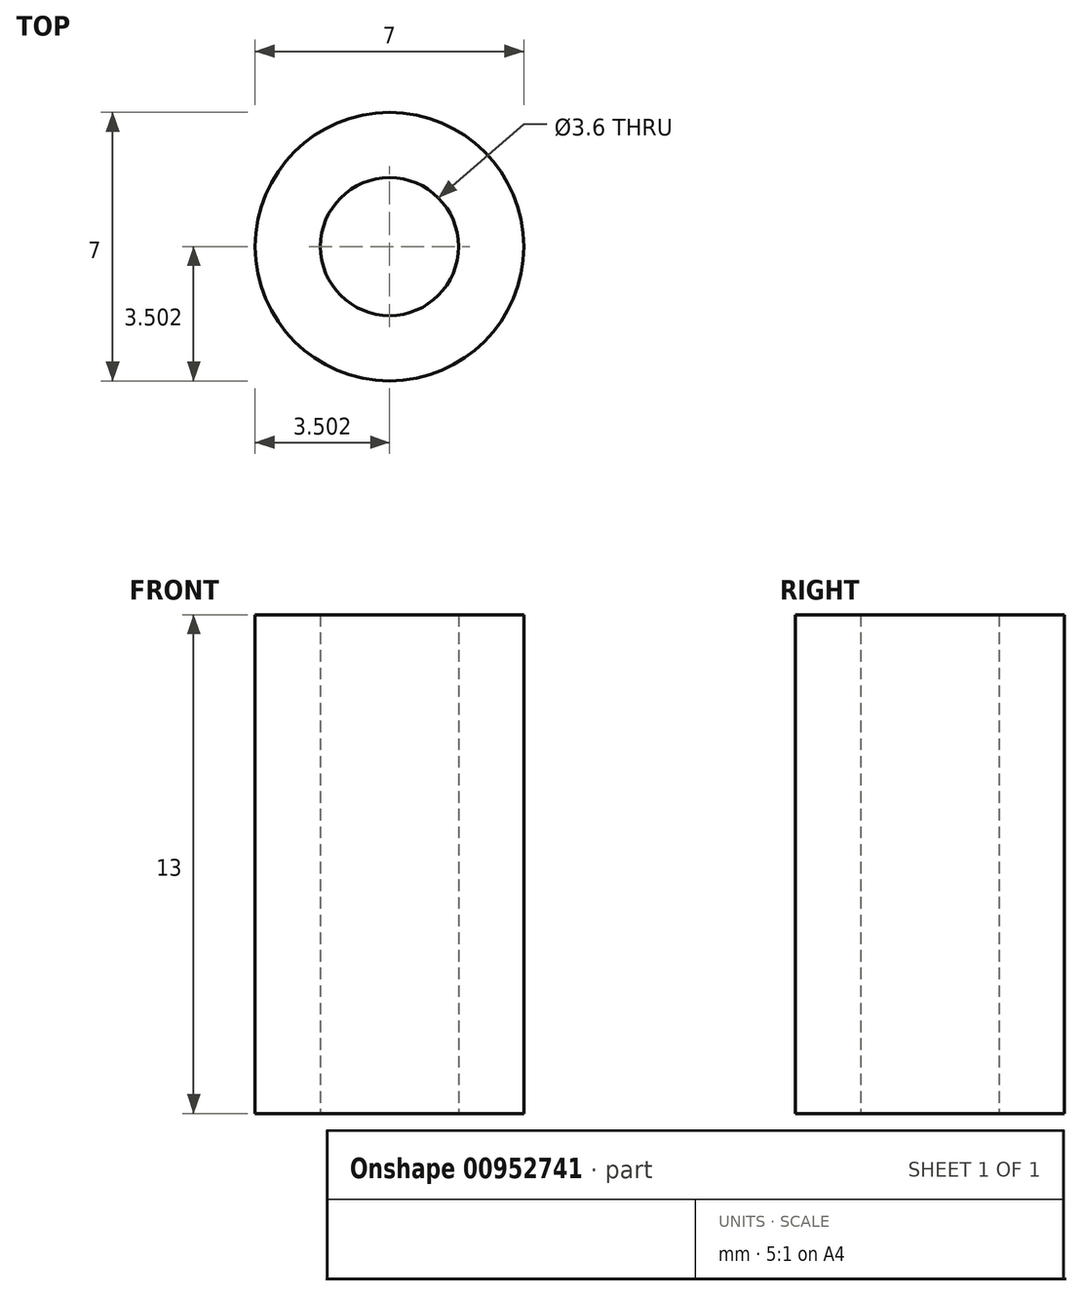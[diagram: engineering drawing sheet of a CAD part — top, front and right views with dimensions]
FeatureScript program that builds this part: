
annotation { "Feature Type Name" : "Feature", "Feature Type Description" : "" }
export const myFeature = defineFeature(function(context is Context, id is Id, definition is map)
    precondition{}
    {
        {
            var Q0;
            Q0=qCreatedBy(makeId("Top.planeOp"),FACE);
            var sketch = newSketch(context, id + "F0", { "sketchPlane" : qUnion([Q0])});
            skCircle(sketch, "E0", {"center": v(-38.23, 20.6) * mm, "radius": 1.8 * mm});
            skCircle(sketch, "E1", {"center": v(-38.23, 20.6) * mm, "radius": 3.5 * mm});
            skSolve(sketch);
        }
        {
            var Q0;
            Q0=makeQuery(id+"F0.imprint","IMPRINT",FACE,{"disambiguationData":[TD([[makeQuery(id+"F0.imprint","IMPRINT",EDGE,{"derivedFrom":sQuery(id+"F0.wireOp",EDGE,"E0")}),-1.0]])]});
            extrude(context, id + "F1", {"entities" : qUnion([Q0]), "depth" : 13 * mm, "offsetDistance" : 25 * mm});
        }
    });
